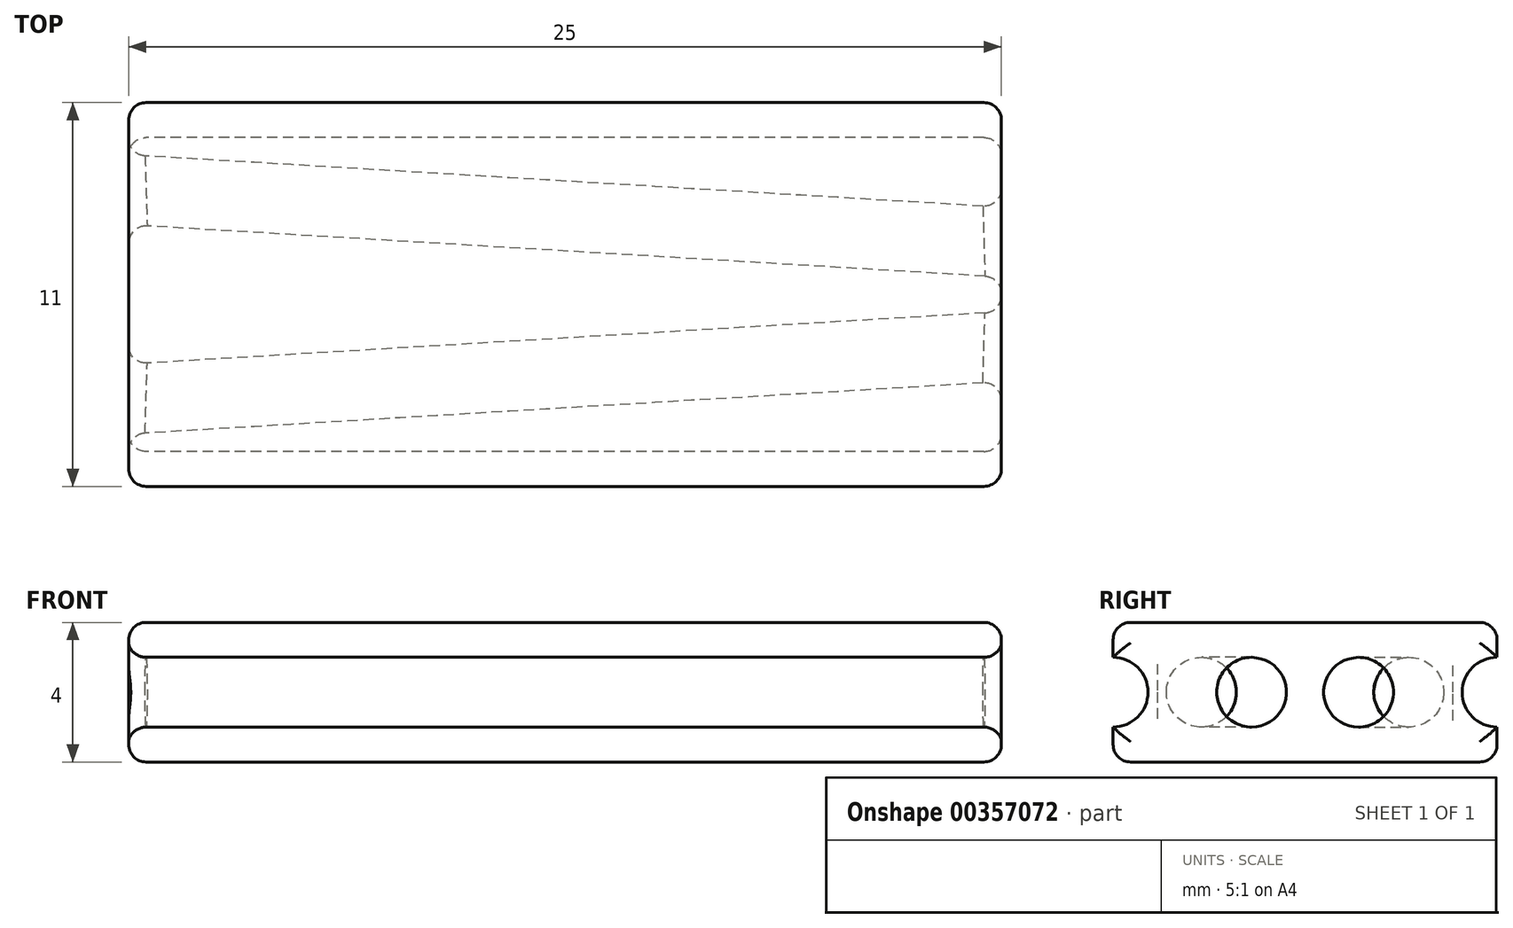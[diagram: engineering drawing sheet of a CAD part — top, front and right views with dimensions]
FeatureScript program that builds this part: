
annotation { "Feature Type Name" : "Feature", "Feature Type Description" : "" }
export const myFeature = defineFeature(function(context is Context, id is Id, definition is map)
    precondition{}
    {
        {
            var Q0;
            Q0=qCreatedBy(makeId("Top.planeOp"),FACE);
            var sketch = newSketch(context, id + "F0", { "sketchPlane" : qUnion([Q0])});
            skLineSegment(sketch, "E0.bottom", {"start": v(-12.5, 5.5) * mm, "end": v(12.5, 5.5) * mm});
            skLineSegment(sketch, "E0.top", {"start": v(-12.5, -5.5) * mm, "end": v(12.5, -5.5) * mm});
            skLineSegment(sketch, "E0.left", {"start": v(-12.5, 5.5) * mm, "end": v(-12.5, -5.5) * mm});
            skLineSegment(sketch, "E0.right", {"start": v(12.5, 5.5) * mm, "end": v(12.5, -5.5) * mm});
            skPoint(sketch, "E1", {"position": v(0, 5.5) * mm});
            skPoint(sketch, "E2", {"position": v(12.5, 0) * mm});
            skSolve(sketch);
        }
        {
            var Q0;
            Q0=qCreatedBy(makeId("Top.planeOp"),FACE);
            var sketch = newSketch(context, id + "F1", { "sketchPlane" : qUnion([Q0])});
            skLineSegment(sketch, "E3", {"start": v(-13.3, 3.05) * mm, "end": v(14.5, 1.38) * mm});
            skPoint(sketch, "E4", {"position": v(-12.5, 3) * mm});
            skPoint(sketch, "E5", {"position": v(12.5, 1.5) * mm});
            skLineSegment(sketch, "E6", {"start": v(-13.3, 4.05) * mm, "end": v(14.5, 2.38) * mm});
            skLineSegment(sketch, "E7", {"start": v(-13.3, 4.05) * mm, "end": v(-13.3, 3.05) * mm});
            skLineSegment(sketch, "E8", {"start": v(14.5, 2.38) * mm, "end": v(14.5, 1.38) * mm});
            skLineSegment(sketch, "E9.0", {"start": v(-12.5, 5.5) * mm, "end": v(12.5, 5.5) * mm});
            skLineSegment(sketch, "E10", {"start": v(12.5, 4.5) * mm, "end": v(-12.5, 4.5) * mm});
            skLineSegment(sketch, "E11", {"start": v(12.5, 4.5) * mm, "end": v(12.5, 5.5) * mm});
            skLineSegment(sketch, "E12", {"start": v(-12.5, 5.5) * mm, "end": v(-12.5, 4.5) * mm});
            skSolve(sketch);
        }
        {
            var Q0;
            Q0=makeQuery(id+"F1.imprint","IMPRINT",FACE,{"disambiguationData":[TD([[makeQuery(id+"F1.imprint","IMPRINT",EDGE,{"derivedFrom":sQuery(id+"F1.wireOp",EDGE,"E3")}),1.0]])]});
            var Q1;
            Q1=sQuery(id+"F1.wireOp",EDGE,"E3");
            revolve(context, id + "F2", {"entities" : qUnion([Q0]), "axis" : qUnion([Q1]), "revolveType" : RevolveType.FULL});
        }
        {
            var Q0;
            {var subQ1=sQuery(id+"F1.wireOp",EDGE,"E9.0");Q0=makeQuery(id+"F1.imprint","IMPRINT",FACE,{"disambiguationData":[TD([[makeQuery(id+"F1.imprint","IMPRINT",EDGE,{"derivedFrom":subQ1}),-1.0]])]});}
            var Q1;
            Q1=sQuery(id+"F0.wireOp",EDGE,"E0.bottom");
            revolve(context, id + "F3", {"entities" : qUnion([Q0]), "axis" : qUnion([Q1]), "revolveType" : RevolveType.FULL});
        }
        {
            var Q0;
            Q0=makeQuery(id+"F2.opRevolve","SWEPT_BODY",BODY,{"disambiguationData":[OSD([sQuery(id+"F1.wireOp",EDGE,"E3"),sQuery(id+"F1.wireOp",EDGE,"E6"),sQuery(id+"F1.wireOp",EDGE,"E7"),sQuery(id+"F1.wireOp",EDGE,"E8")])]});
            var Q1;
            Q1=makeQuery(id+"F3.opRevolve","SWEPT_BODY",BODY,{"disambiguationData":[OSD([sQuery(id+"F1.wireOp",EDGE,"E6"),sQuery(id+"F1.wireOp",EDGE,"E9.0"),sQuery(id+"F1.wireOp",EDGE,"E10"),sQuery(id+"F1.wireOp",EDGE,"E11"),sQuery(id+"F1.wireOp",EDGE,"E12")])]});
            var Q2;
            Q2=qCreatedBy(makeId("Front.planeOp"),FACE);
            mirror(context, id + "F4", {"entities" : qUnion([Q0, Q1]), "mirrorPlane" : qUnion([Q2])});
        }
        {
            var Q0;
            Q0 = qSketchRegion(id + "F0", true);
            extrude(context, id + "F5", {"entities" : qUnion([Q0]), "endBound" : BoundingType.SYMMETRIC, "depth" : 4 * mm, "offsetDistance" : 25 * mm});
        }
        {
            var Q0;
            Q0=makeQuery(id+"F4.opPattern","COPY",BODY,{"derivedFrom":makeQuery(id+"F2.opRevolve","SWEPT_BODY",BODY,{"disambiguationData":[OSD([sQuery(id+"F1.wireOp",EDGE,"E3"),sQuery(id+"F1.wireOp",EDGE,"E6"),sQuery(id+"F1.wireOp",EDGE,"E7"),sQuery(id+"F1.wireOp",EDGE,"E8")])]}),"instanceName":"1"});
            var Q1;
            Q1=makeQuery(id+"F4.opPattern","COPY",BODY,{"derivedFrom":makeQuery(id+"F3.opRevolve","SWEPT_BODY",BODY,{"disambiguationData":[OSD([sQuery(id+"F1.wireOp",EDGE,"E6"),sQuery(id+"F1.wireOp",EDGE,"E9.0"),sQuery(id+"F1.wireOp",EDGE,"E10"),sQuery(id+"F1.wireOp",EDGE,"E11"),sQuery(id+"F1.wireOp",EDGE,"E12")])]}),"instanceName":"1"});
            var Q2;
            Q2=makeQuery(id+"F2.opRevolve","SWEPT_BODY",BODY,{"disambiguationData":[OSD([sQuery(id+"F1.wireOp",EDGE,"E3"),sQuery(id+"F1.wireOp",EDGE,"E6"),sQuery(id+"F1.wireOp",EDGE,"E7"),sQuery(id+"F1.wireOp",EDGE,"E8")])]});
            var Q3;
            Q3=makeQuery(id+"F3.opRevolve","SWEPT_BODY",BODY,{"disambiguationData":[OSD([sQuery(id+"F1.wireOp",EDGE,"E9.0"),sQuery(id+"F1.wireOp",EDGE,"E10"),sQuery(id+"F1.wireOp",EDGE,"E11"),sQuery(id+"F1.wireOp",EDGE,"E12")])]});
            var Q4;
            Q4=makeQuery(id+"F5.opExtrude","SWEPT_BODY",BODY,{"disambiguationData":[OSD([sQuery(id+"F0.wireOp",EDGE,"E0.bottom"),sQuery(id+"F0.wireOp",EDGE,"E0.top"),sQuery(id+"F0.wireOp",EDGE,"E0.left"),sQuery(id+"F0.wireOp",EDGE,"E0.right")])]});
            booleanBodies(context, id + "F6", {"operationType" : BooleanOperationType.SUBTRACTION, "tools" : qUnion([Q0, Q1, Q2, Q3]), "targets" : qUnion([Q4])});
        }
        {
            var Q0;
            Q0=makeQuery(id+"F5.opExtrude","CAP_FACE",FACE,{"disambiguationData":[OSD([sQuery(id+"F0.wireOp",EDGE,"E0.bottom"),sQuery(id+"F0.wireOp",EDGE,"E0.top"),sQuery(id+"F0.wireOp",EDGE,"E0.left"),sQuery(id+"F0.wireOp",EDGE,"E0.right")])],"isStart":true});
            var Q1;
            Q1=makeQuery(id+"F5.opExtrude","CAP_FACE",FACE,{"disambiguationData":[OSD([sQuery(id+"F0.wireOp",EDGE,"E0.bottom"),sQuery(id+"F0.wireOp",EDGE,"E0.top"),sQuery(id+"F0.wireOp",EDGE,"E0.left"),sQuery(id+"F0.wireOp",EDGE,"E0.right")])],"isStart":false});
            var Q2;
            Q2=makeQuery(id+"F5.opExtrude","SWEPT_FACE",FACE,{"disambiguationData":[OSD([sQuery(id+"F0.wireOp",EDGE,"E0.right")])]});
            var Q3;
            Q3=makeQuery(id+"F5.opExtrude","SWEPT_FACE",FACE,{"disambiguationData":[OSD([sQuery(id+"F0.wireOp",EDGE,"E0.left")])]});
            fillet(context, id + "F7", {"entities" : qUnion([Q0, Q1, Q2, Q3]), "radius" : 0.5 * mm, "tangentPropagation" : true, "allowEdgeOverflow" : false});
        }
    });
